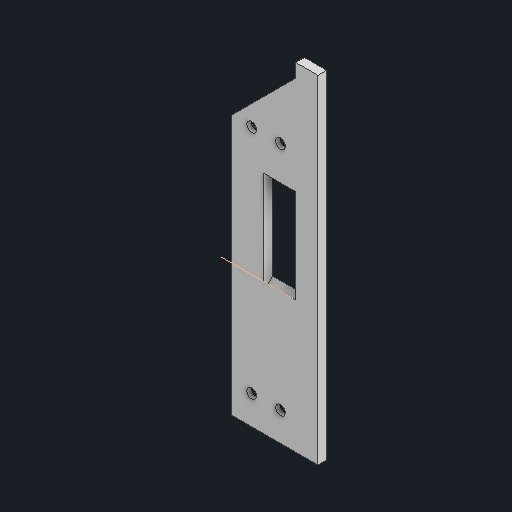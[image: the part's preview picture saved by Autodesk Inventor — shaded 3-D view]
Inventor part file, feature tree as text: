
AUTODESK INVENTOR PART (.ipt)
format: ipt  version: 2023 (Build 270158000, 158)  size: 117,248 bytes
history: native  units: in
note: dims shown in document units (in); Inventor stores cm internally (conversion verified against a paired STEP export)
features: other x3, sketch x3
ambient origin geometry x8: Origin, YZ Plane, XZ Plane, XY Plane, X Axis, Y Axis, Z Axis, Center Point
bodies: Solid1 (feature_tree)
feature tree (6):
  other  "BokPrawy.ipt"
  other  "Solid1::BokPrawy.ipt"
  other  "TaggingFeature1"
  sketch  "Sketch1"  dims[d0=0.3937in]
  sketch  "Sketch3"
  sketch  "Sketch4"
